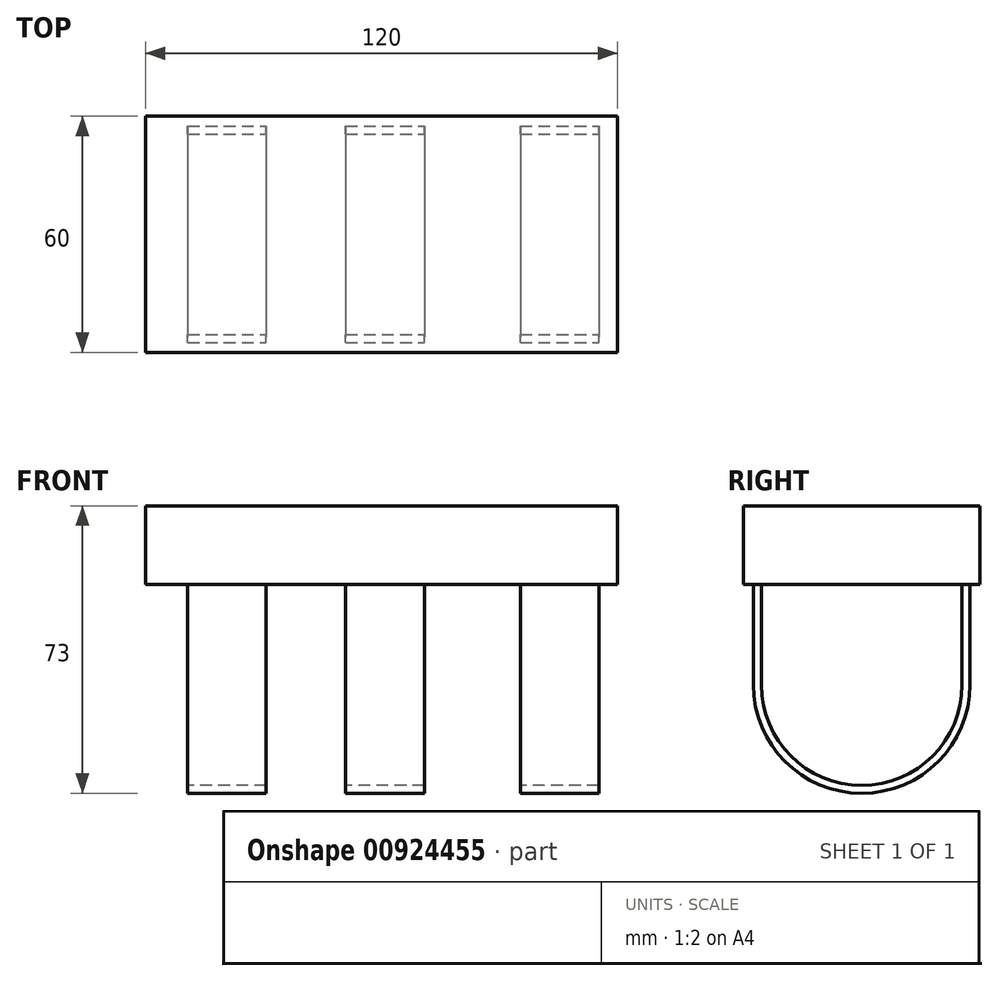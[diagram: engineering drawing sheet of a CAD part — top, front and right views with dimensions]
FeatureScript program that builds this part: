
annotation { "Feature Type Name" : "Feature", "Feature Type Description" : "" }
export const myFeature = defineFeature(function(context is Context, id is Id, definition is map)
    precondition{}
    {
        {
            var Q0;
            Q0=qCreatedBy(makeId("Top.planeOp"),FACE);
            var sketch = newSketch(context, id + "F0", { "sketchPlane" : qUnion([Q0])});
            skLineSegment(sketch, "E0.bottom", {"start": v(-60, 30) * mm, "end": v(60, 30) * mm});
            skLineSegment(sketch, "E0.top", {"start": v(-60, -30) * mm, "end": v(60, -30) * mm});
            skLineSegment(sketch, "E0.left", {"start": v(-60, 30) * mm, "end": v(-60, -30) * mm});
            skLineSegment(sketch, "E0.right", {"start": v(60, 30) * mm, "end": v(60, -30) * mm});
            skSolve(sketch);
        }
        {
            var Q0;
            Q0=qSketchRegion(id+"F0",true);
            var Q1;
            Q1=qSketchRegion(id+"F2",true);
            extrude(context, id + "F1", {"entities" : qUnion([Q0, Q1]), "depth" : 20 * mm, "offsetDistance" : 25 * mm});
        }
        {
            var Q0;
            Q0=makeQuery(id+"F1.opExtrude","CAP_FACE",FACE,{"disambiguationData":[OSD([sQuery(id+"F0.wireOp",EDGE,"E0.bottom"),sQuery(id+"F0.wireOp",EDGE,"E0.top"),sQuery(id+"F0.wireOp",EDGE,"E0.left"),sQuery(id+"F0.wireOp",EDGE,"E0.right")])],"isStart":true});
            var sketch = newSketch(context, id + "F2", { "sketchPlane" : qUnion([Q0])});
            skLineSegment(sketch, "E1.bottom", {"start": v(-49.28, 27.5) * mm, "end": v(-29.28, 27.5) * mm});
            skLineSegment(sketch, "E1.top", {"start": v(-49.28, 25.5) * mm, "end": v(-29.28, 25.5) * mm});
            skLineSegment(sketch, "E1.left", {"start": v(-49.28, 27.5) * mm, "end": v(-49.28, 25.5) * mm});
            skLineSegment(sketch, "E1.right", {"start": v(-29.28, 27.5) * mm, "end": v(-29.28, 25.5) * mm});
            skLineSegment(sketch, "E2.bottom", {"start": v(-9.1, 27.5) * mm, "end": v(10.9, 27.5) * mm});
            skLineSegment(sketch, "E2.top", {"start": v(-9.1, 25.5) * mm, "end": v(10.9, 25.5) * mm});
            skLineSegment(sketch, "E2.left", {"start": v(-9.1, 27.5) * mm, "end": v(-9.1, 25.5) * mm});
            skLineSegment(sketch, "E2.right", {"start": v(10.9, 27.5) * mm, "end": v(10.9, 25.5) * mm});
            skLineSegment(sketch, "E3.bottom", {"start": v(35.25, 27.5) * mm, "end": v(55.25, 27.5) * mm});
            skLineSegment(sketch, "E3.top", {"start": v(35.25, 25.5) * mm, "end": v(55.25, 25.5) * mm});
            skLineSegment(sketch, "E3.left", {"start": v(35.25, 27.5) * mm, "end": v(35.25, 25.5) * mm});
            skLineSegment(sketch, "E3.right", {"start": v(55.25, 27.5) * mm, "end": v(55.25, 25.5) * mm});
            skLineSegment(sketch, "E4.bottom", {"start": v(-49.28, -25.5) * mm, "end": v(-29.28, -25.5) * mm});
            skLineSegment(sketch, "E4.top", {"start": v(-49.28, -27.5) * mm, "end": v(-29.28, -27.5) * mm});
            skLineSegment(sketch, "E4.left", {"start": v(-49.28, -25.5) * mm, "end": v(-49.28, -27.5) * mm});
            skLineSegment(sketch, "E4.right", {"start": v(-29.28, -25.5) * mm, "end": v(-29.28, -27.5) * mm});
            skLineSegment(sketch, "E5.bottom", {"start": v(-9.1, -25.5) * mm, "end": v(10.9, -25.5) * mm});
            skLineSegment(sketch, "E5.top", {"start": v(-9.1, -27.5) * mm, "end": v(10.9, -27.5) * mm});
            skLineSegment(sketch, "E5.left", {"start": v(-9.1, -25.5) * mm, "end": v(-9.1, -27.5) * mm});
            skLineSegment(sketch, "E5.right", {"start": v(10.9, -25.5) * mm, "end": v(10.9, -27.5) * mm});
            skLineSegment(sketch, "E6.bottom", {"start": v(35.25, -25.5) * mm, "end": v(55.25, -25.5) * mm});
            skLineSegment(sketch, "E6.top", {"start": v(35.25, -27.5) * mm, "end": v(55.25, -27.5) * mm});
            skLineSegment(sketch, "E6.left", {"start": v(35.25, -25.5) * mm, "end": v(35.25, -27.5) * mm});
            skLineSegment(sketch, "E6.right", {"start": v(55.25, -25.5) * mm, "end": v(55.25, -27.5) * mm});
            skSolve(sketch);
        }
        {
            var Q0;
            Q0=makeQuery(id+"F2.imprint","IMPRINT",FACE,{"disambiguationData":[TD([[makeQuery(id+"F2.imprint","IMPRINT",EDGE,{"derivedFrom":sQuery(id+"F2.wireOp",EDGE,"E1.bottom")}),-1.0]])]});
            var Q1;
            Q1=makeQuery(id+"F2.imprint","IMPRINT",FACE,{"disambiguationData":[TD([[makeQuery(id+"F2.imprint","IMPRINT",EDGE,{"derivedFrom":sQuery(id+"F2.wireOp",EDGE,"E4.bottom")}),-1.0]])]});
            var Q2;
            Q2=makeQuery(id+"F2.imprint","IMPRINT",FACE,{"disambiguationData":[TD([[makeQuery(id+"F2.imprint","IMPRINT",EDGE,{"derivedFrom":sQuery(id+"F2.wireOp",EDGE,"E2.bottom")}),-1.0]])]});
            var Q3;
            Q3=makeQuery(id+"F2.imprint","IMPRINT",FACE,{"disambiguationData":[TD([[makeQuery(id+"F2.imprint","IMPRINT",EDGE,{"derivedFrom":sQuery(id+"F2.wireOp",EDGE,"E5.bottom")}),-1.0]])]});
            var Q4;
            Q4=makeQuery(id+"F2.imprint","IMPRINT",FACE,{"disambiguationData":[TD([[makeQuery(id+"F2.imprint","IMPRINT",EDGE,{"derivedFrom":sQuery(id+"F2.wireOp",EDGE,"E3.bottom")}),-1.0]])]});
            var Q5;
            Q5=makeQuery(id+"F2.imprint","IMPRINT",FACE,{"disambiguationData":[TD([[makeQuery(id+"F2.imprint","IMPRINT",EDGE,{"derivedFrom":sQuery(id+"F2.wireOp",EDGE,"E6.bottom")}),-1.0]])]});
            extrude(context, id + "F3", {"entities" : qUnion([Q0, Q1, Q2, Q3, Q4, Q5]), "operationType" : NewBodyOperationType.ADD, "depth" : 25.5 * mm, "offsetDistance" : 25 * mm});
        }
        {
            var Q0;
            Q0=makeQuery(id+"F3.opExtrude","CAP_FACE",FACE,{"disambiguationData":[OSD([sQuery(id+"F2.wireOp",EDGE,"E1.bottom"),sQuery(id+"F2.wireOp",EDGE,"E1.top"),sQuery(id+"F2.wireOp",EDGE,"E1.left"),sQuery(id+"F2.wireOp",EDGE,"E1.right")])],"isStart":false});
            var sketch = newSketch(context, id + "F4", { "sketchPlane" : qUnion([Q0])});
            skLineSegment(sketch, "E7", {"start": v(-65.3, 0) * mm, "end": v(69.27, 0) * mm});
            skSolve(sketch);
        }
        {
            var Q0;
            Q0=qSketchRegion(id+"F4",true);
            var Q1;
            Q1=makeQuery(id+"F4.imprint","IMPRINT",FACE,{"disambiguationData":[TD([[makeQuery(id+"F4.imprint","IMPRINT",EDGE,{"derivedFrom":makeQuery(id+"F3.opExtrude","CAP_EDGE",EDGE,{"disambiguationData":[OSD([sQuery(id+"F2.wireOp",EDGE,"E1.bottom")])],"isStart":false})}),-1.0]])]});
            var Q2;
            Q2=makeQuery(id+"F3.opExtrude","CAP_FACE",FACE,{"disambiguationData":[OSD([sQuery(id+"F2.wireOp",EDGE,"E2.bottom"),sQuery(id+"F2.wireOp",EDGE,"E2.top"),sQuery(id+"F2.wireOp",EDGE,"E2.left"),sQuery(id+"F2.wireOp",EDGE,"E2.right")])],"isStart":false});
            var Q3;
            Q3=makeQuery(id+"F3.opExtrude","CAP_FACE",FACE,{"disambiguationData":[OSD([sQuery(id+"F2.wireOp",EDGE,"E3.bottom"),sQuery(id+"F2.wireOp",EDGE,"E3.top"),sQuery(id+"F2.wireOp",EDGE,"E3.left"),sQuery(id+"F2.wireOp",EDGE,"E3.right")])],"isStart":false});
            var Q4;
            Q4=sQuery(id+"F4.wireOp",EDGE,"E7");
            revolve(context, id + "F5", {"operationType" : NewBodyOperationType.ADD, "surfaceOperationType" : NewSurfaceOperationType.NEW, "entities" : qUnion([Q0, Q1, Q2, Q3]), "axis" : qUnion([Q4]), "revolveType" : RevolveType.ONE_DIRECTION, "angle" : 180 * degree});
        }
    });
